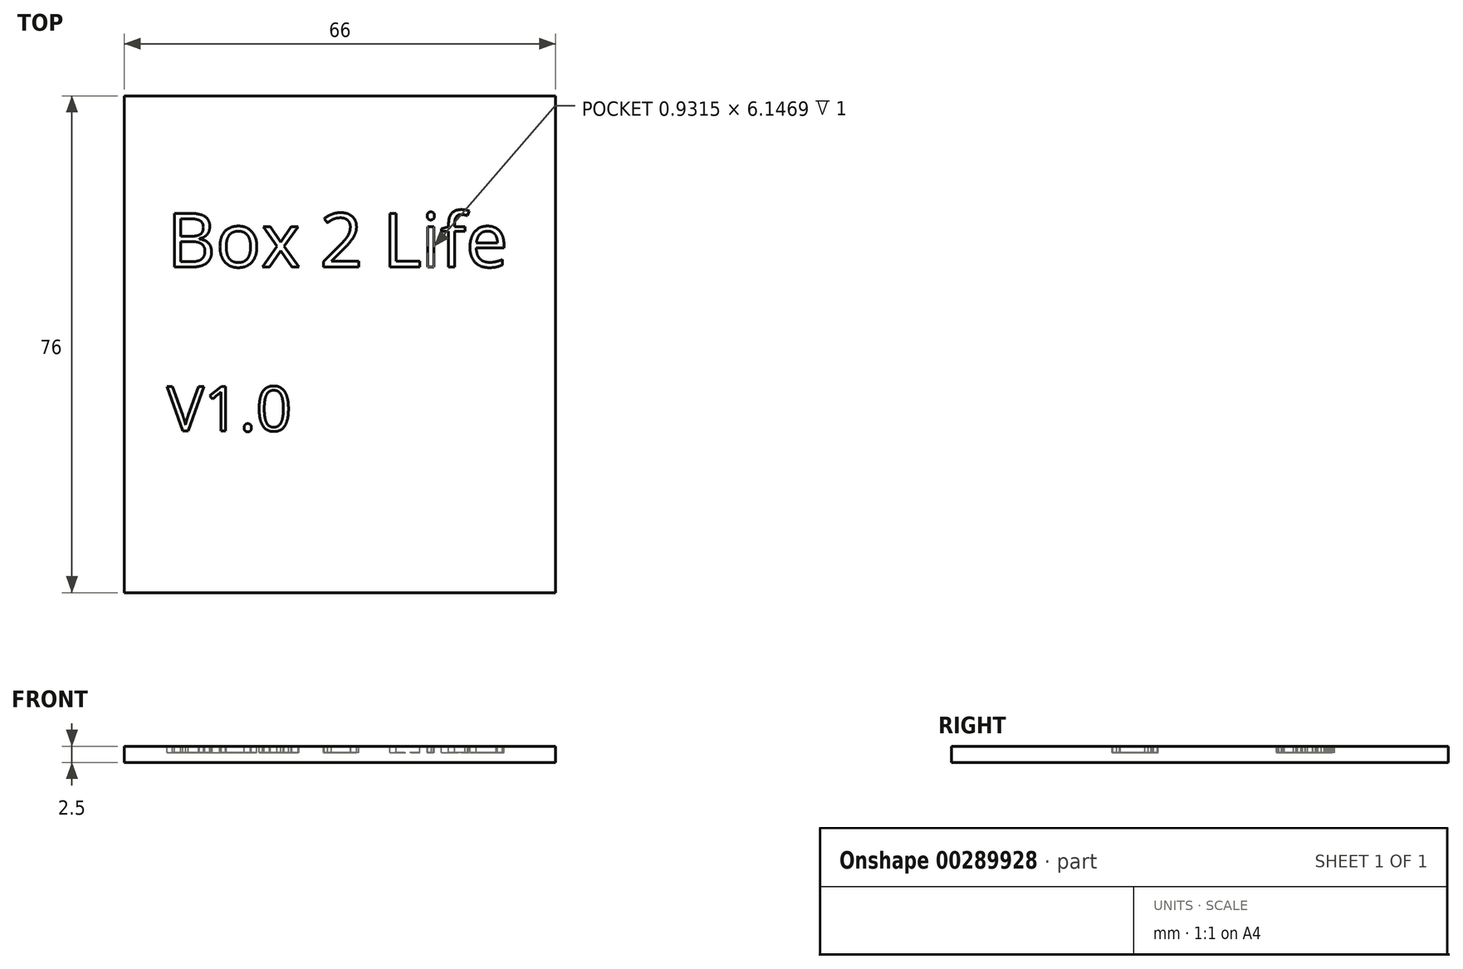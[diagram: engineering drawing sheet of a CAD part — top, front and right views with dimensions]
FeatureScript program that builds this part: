
annotation { "Feature Type Name" : "Feature", "Feature Type Description" : "" }
export const myFeature = defineFeature(function(context is Context, id is Id, definition is map)
    precondition{}
    {
        {
            var Q0;
            Q0=qCreatedBy(makeId("Top.planeOp"),FACE);
            var sketch = newSketch(context, id + "F0", { "sketchPlane" : qUnion([Q0])});
            skLineSegment(sketch, "E0.bottom", {"start": v(0, 0) * mm, "end": v(66, 0) * mm});
            skLineSegment(sketch, "E0.top", {"start": v(0, 76) * mm, "end": v(66, 76) * mm});
            skLineSegment(sketch, "E0.left", {"start": v(0, 0) * mm, "end": v(0, 76) * mm});
            skLineSegment(sketch, "E0.right", {"start": v(66, 0) * mm, "end": v(66, 76) * mm});
            skSolve(sketch);
        }
        {
            var Q0;
            Q0 = qSketchRegion(id + "F0", true);
            extrude(context, id + "F1", {"entities" : qUnion([Q0]), "depth" : 2.5 * mm});
        }
        {
            var Q0;
            Q0=makeQuery(id+"F1.opExtrude","CAP_FACE",FACE,{"disambiguationData":[OSD([sQuery(id+"F0.wireOp",EDGE,"E0.bottom"),sQuery(id+"F0.wireOp",EDGE,"E0.top"),sQuery(id+"F0.wireOp",EDGE,"E0.left"),sQuery(id+"F0.wireOp",EDGE,"E0.right")])],"isStart":false});
            var sketch = newSketch(context, id + "F2", { "sketchPlane" : qUnion([Q0])});
            skText(sketch, "E1", { "text": "Box 2 Life", "fontName": "OpenSans-Regular.ttf"});
            skText(sketch, "E2", { "text": "V1.0", "fontName": "OpenSans-Regular.ttf"});
            const initialGuessF2  = {"E1": [0.00656, 0.04983, 1, 0, 0.00827], "E2": [0.00656, 0.02474, 1, 0, 0.00684]};
            skSetInitialGuess(sketch, initialGuessF2);
            skSolve(sketch);
        }
        {
            var Q0;
            Q0 = qSketchRegion(id + "F2", true);
            extrude(context, id + "F3", {"entities" : qUnion([Q0]), "operationType" : NewBodyOperationType.REMOVE, "oppositeDirection" : true, "depth" : 1 * mm});
        }
    });
